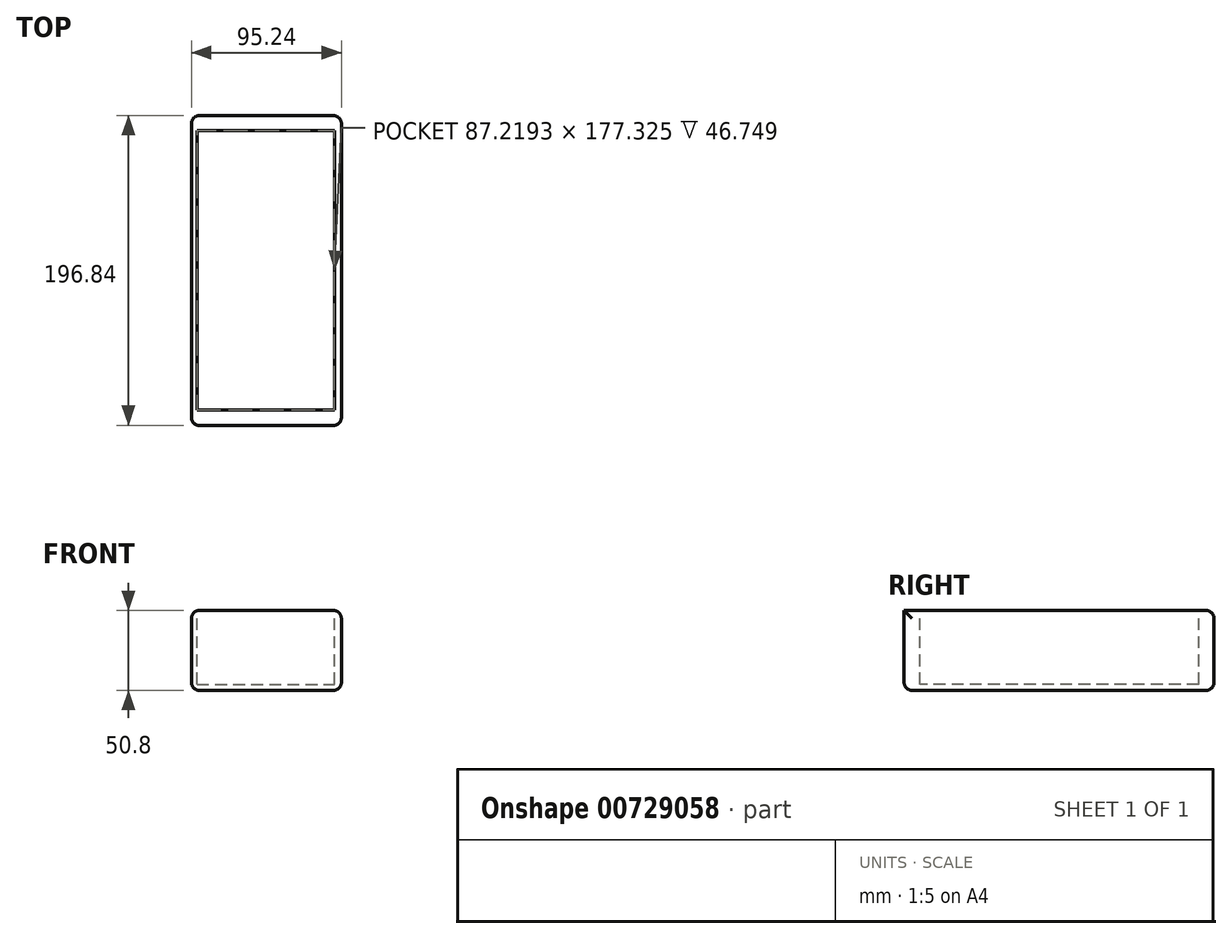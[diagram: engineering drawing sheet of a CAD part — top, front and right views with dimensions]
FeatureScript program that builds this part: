
annotation { "Feature Type Name" : "Feature", "Feature Type Description" : "" }
export const myFeature = defineFeature(function(context is Context, id is Id, definition is map)
    precondition{}
    {
        {
            var Q0;
            Q0=qCreatedBy(makeId("Top.planeOp"),FACE);
            var sketch = newSketch(context, id + "F0", { "sketchPlane" : qUnion([Q0])});
            skLineSegment(sketch, "E0.bottom", {"start": v(-47.63, 98.42) * mm, "end": v(47.63, 98.43) * mm});
            skLineSegment(sketch, "E0.top", {"start": v(-47.63, -98.43) * mm, "end": v(47.63, -98.42) * mm});
            skLineSegment(sketch, "E0.left", {"start": v(-47.63, 98.42) * mm, "end": v(-47.63, -98.43) * mm});
            skLineSegment(sketch, "E0.right", {"start": v(47.63, 98.43) * mm, "end": v(47.63, -98.42) * mm});
            skPoint(sketch, "E0.middle", {"position": v(0, 0) * mm});
            skSolve(sketch);
        }
        {
            var Q0;
            Q0=makeQuery(id+"F0.imprint","IMPRINT",FACE,{"disambiguationData":[TD([[makeQuery(id+"F0.imprint","IMPRINT",EDGE,{"derivedFrom":sQuery(id+"F0.wireOp",EDGE,"E0.bottom")}),-1.0]])]});
            extrude(context, id + "F1", {"entities" : qUnion([Q0]), "depth" : 50.8 * mm, "offsetDistance" : 25.4 * mm});
        }
        {
            var Q0;
            Q0=makeQuery(id+"F1.opExtrude","CAP_FACE",FACE,{"disambiguationData":[OSD([sQuery(id+"F0.wireOp",EDGE,"E0.bottom"),sQuery(id+"F0.wireOp",EDGE,"E0.top"),sQuery(id+"F0.wireOp",EDGE,"E0.left"),sQuery(id+"F0.wireOp",EDGE,"E0.right")])],"isStart":false});
            var sketch = newSketch(context, id + "F2", { "sketchPlane" : qUnion([Q0])});
            skLineSegment(sketch, "E1.bottom", {"start": v(-44.1, 88.82) * mm, "end": v(43.13, 88.82) * mm});
            skLineSegment(sketch, "E1.top", {"start": v(-44.1, -88.5) * mm, "end": v(43.13, -88.5) * mm});
            skLineSegment(sketch, "E1.left", {"start": v(-44.1, 88.82) * mm, "end": v(-44.1, -88.5) * mm});
            skLineSegment(sketch, "E1.right", {"start": v(43.13, 88.82) * mm, "end": v(43.13, -88.5) * mm});
            skSolve(sketch);
        }
        {
            var Q0;
            Q0 = qSketchRegion(id + "F2", true);
            extrude(context, id + "F3", {"entities" : qUnion([Q0]), "operationType" : NewBodyOperationType.REMOVE, "oppositeDirection" : true, "depth" : 47 * mm, "offsetDistance" : 25.4 * mm});
        }
        {
            var Q0;
            Q0=makeQuery(id+"F1.opExtrude","CAP_EDGE",EDGE,{"disambiguationData":[OSD([sQuery(id+"F0.wireOp",EDGE,"E0.left")])],"isStart":false});
            var Q1;
            Q1=makeQuery(id+"F1.opExtrude","CAP_EDGE",EDGE,{"disambiguationData":[OSD([sQuery(id+"F0.wireOp",EDGE,"E0.bottom")])],"isStart":false});
            var Q2;
            Q2=makeQuery(id+"F1.opExtrude","CAP_EDGE",EDGE,{"disambiguationData":[OSD([sQuery(id+"F0.wireOp",EDGE,"E0.right")])],"isStart":false});
            var Q3;
            Q3=makeQuery(id+"F1.opExtrude","SWEPT_EDGE",EDGE,{"disambiguationData":[OSD([sQuery(id+"F0.wireOp",EDGE,"E0.bottom"),sQuery(id+"F0.wireOp",EDGE,"E0.left")])]});
            var Q4;
            Q4=makeQuery(id+"F1.opExtrude","CAP_EDGE",EDGE,{"disambiguationData":[OSD([sQuery(id+"F0.wireOp",EDGE,"E0.left")])],"isStart":true});
            var Q5;
            Q5=makeQuery(id+"F1.opExtrude","SWEPT_EDGE",EDGE,{"disambiguationData":[OSD([sQuery(id+"F0.wireOp",EDGE,"E0.top"),sQuery(id+"F0.wireOp",EDGE,"E0.left")])]});
            var Q6;
            Q6=makeQuery(id+"F1.opExtrude","CAP_EDGE",EDGE,{"disambiguationData":[OSD([sQuery(id+"F0.wireOp",EDGE,"E0.top")])],"isStart":true});
            var Q7;
            Q7=makeQuery(id+"F3.boolean.opBoolean","COPY",EDGE,{"derivedFrom":makeQuery(id+"F3.opExtrude","CAP_EDGE",EDGE,{"disambiguationData":[OSD([sQuery(id+"F2.wireOp",EDGE,"E1.bottom")])],"isStart":true})});
            var Q8;
            Q8=makeQuery(id+"F3.boolean.opBoolean","COPY",EDGE,{"derivedFrom":makeQuery(id+"F3.opExtrude","CAP_EDGE",EDGE,{"disambiguationData":[OSD([sQuery(id+"F2.wireOp",EDGE,"E1.left")])],"isStart":true})});
            var Q9;
            Q9=makeQuery(id+"F3.boolean.opBoolean","COPY",EDGE,{"derivedFrom":makeQuery(id+"F3.opExtrude","CAP_EDGE",EDGE,{"disambiguationData":[OSD([sQuery(id+"F2.wireOp",EDGE,"E1.right")])],"isStart":true})});
            var Q10;
            Q10=makeQuery(id+"F3.boolean.opBoolean","COPY",EDGE,{"derivedFrom":makeQuery(id+"F3.opExtrude","CAP_EDGE",EDGE,{"disambiguationData":[OSD([sQuery(id+"F2.wireOp",EDGE,"E1.top")])],"isStart":true})});
            var Q11;
            Q11=makeQuery(id+"F1.opExtrude","SWEPT_EDGE",EDGE,{"disambiguationData":[OSD([sQuery(id+"F0.wireOp",EDGE,"E0.top"),sQuery(id+"F0.wireOp",EDGE,"E0.right")])]});
            var Q12;
            Q12=makeQuery(id+"F1.opExtrude","CAP_EDGE",EDGE,{"disambiguationData":[OSD([sQuery(id+"F0.wireOp",EDGE,"E0.bottom")])],"isStart":true});
            var Q13;
            Q13=makeQuery(id+"F1.opExtrude","SWEPT_EDGE",EDGE,{"disambiguationData":[OSD([sQuery(id+"F0.wireOp",EDGE,"E0.bottom"),sQuery(id+"F0.wireOp",EDGE,"E0.right")])]});
            var Q14;
            Q14=makeQuery(id+"F1.opExtrude","CAP_EDGE",EDGE,{"disambiguationData":[OSD([sQuery(id+"F0.wireOp",EDGE,"E0.right")])],"isStart":true});
            fillet(context, id + "F4", {"entities" : qUnion([Q0, Q1, Q2, Q3, Q4, Q5, Q6, Q7, Q8, Q9, Q10, Q11, Q12, Q13, Q14]), "radius" : 5.08 * mm, "tangentPropagation" : true, "allowEdgeOverflow" : false});
        }
    });
